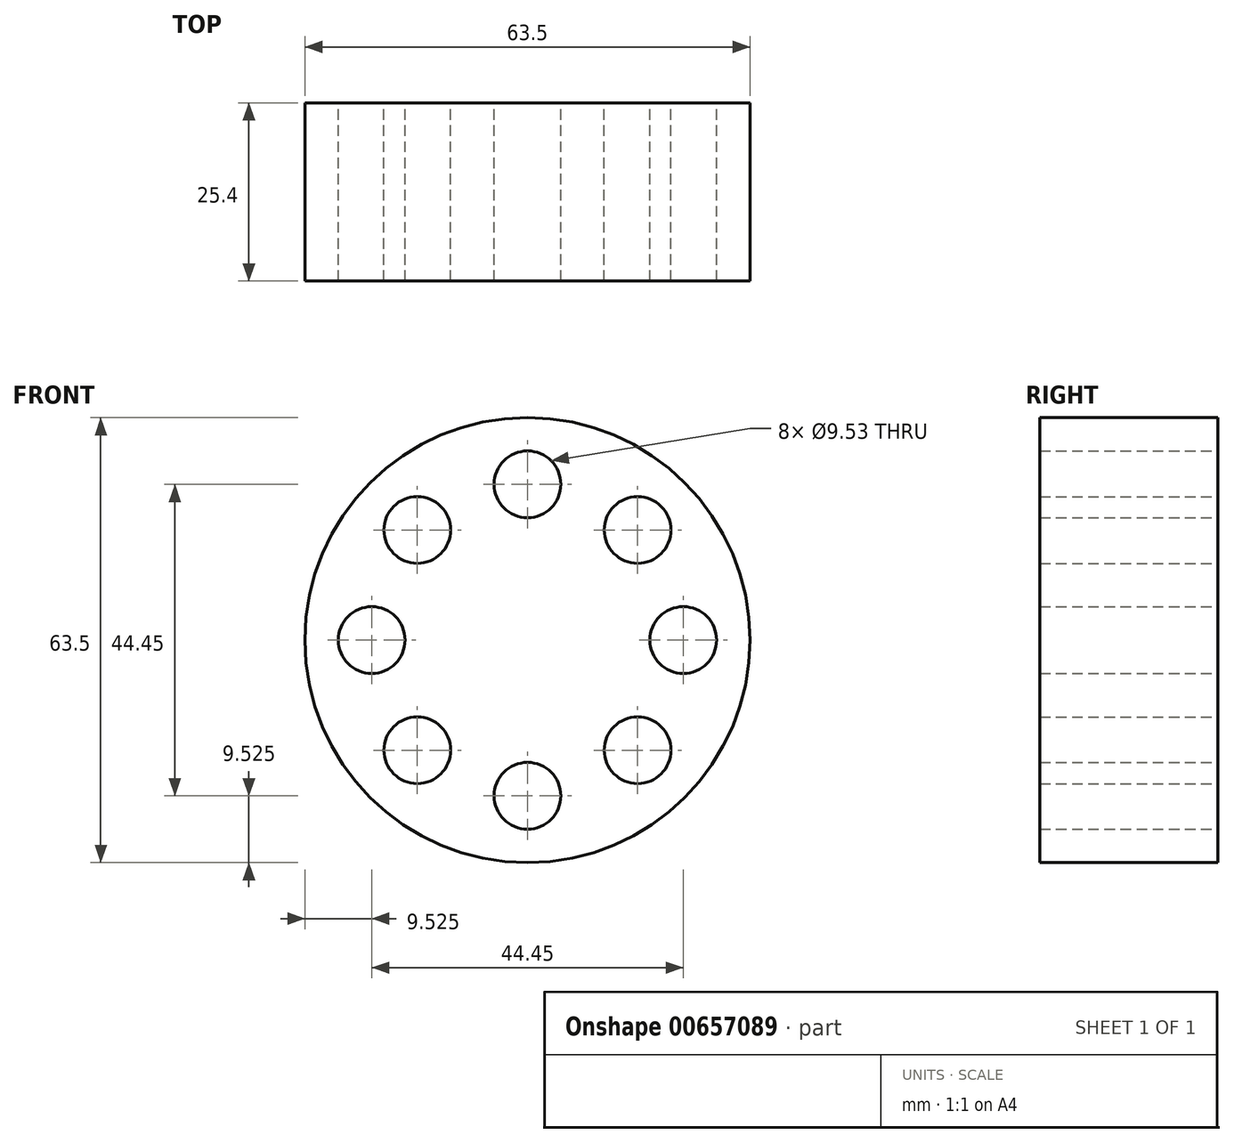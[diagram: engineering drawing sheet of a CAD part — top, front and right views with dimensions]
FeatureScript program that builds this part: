
annotation { "Feature Type Name" : "Feature", "Feature Type Description" : "" }
export const myFeature = defineFeature(function(context is Context, id is Id, definition is map)
    precondition{}
    {
        {
            var Q0;
            Q0=qCreatedBy(makeId("Front.planeOp"),FACE);
            var sketch = newSketch(context, id + "F0", { "sketchPlane" : qUnion([Q0])});
            skCircle(sketch, "E0", {"center": v(0, 0) * mm, "radius": 31.75 * mm});
            skCircle(sketch, "E1", {"center": v(0, 0) * mm, "radius": 22.23 * mm});
            skCircle(sketch, "E2", {"center": v(0, 22.23) * mm, "radius": 4.76 * mm});
            skCircle(sketch, "E3.1.0", {"center": v(-15.72, 15.72) * mm, "radius": 4.76 * mm});
            skCircle(sketch, "E3.2.0", {"center": v(-22.23, 0) * mm, "radius": 4.76 * mm});
            skCircle(sketch, "E4.1.3.0", {"center": v(-15.72, -15.72) * mm, "radius": 4.76 * mm});
            skCircle(sketch, "E4.1.4.0", {"center": v(0, -22.23) * mm, "radius": 4.76 * mm});
            skCircle(sketch, "E4.1.5.0", {"center": v(15.72, -15.72) * mm, "radius": 4.76 * mm});
            skCircle(sketch, "E4.1.6.0", {"center": v(22.23, 0) * mm, "radius": 4.76 * mm});
            skCircle(sketch, "E4.1.7.0", {"center": v(15.72, 15.72) * mm, "radius": 4.76 * mm});
            skSolve(sketch);
        }
        {
            var Q0;
            Q0=makeQuery(id+"F0.imprint","IMPRINT",FACE,{"disambiguationData":[TD([[makeQuery(id+"F0.imprint","IMPRINT",EDGE,{"derivedFrom":sQuery(id+"F0.wireOp",EDGE,"E0")}),1.0]])]});
            var Q1;
            {var subQ1=sQuery(id+"F0.wireOp",EDGE,"E1");var subQ20=sQuery(id+"F0.wireOp",EDGE,"E4.1.7.0");var subQ21=makeQuery(id+"F0.imprint","INTERSECT",VERTEX,{"disambiguationData":[OD(0.0)],"derivedFrom":[subQ1,subQ20]});Q1=makeQuery(id+"F0.imprint","IMPRINT",FACE,{"disambiguationData":[TD([[makeQuery(id+"F0.imprint","IMPRINT",EDGE,{"disambiguationData":[TD([[subQ21,1.0]])],"derivedFrom":subQ1}),1.0]])]});}
            extrude(context, id + "F1", {"entities" : qUnion([Q0, Q1]), "depth" : 25.4 * mm, "offsetDistance" : 25.4 * mm});
        }
    });
